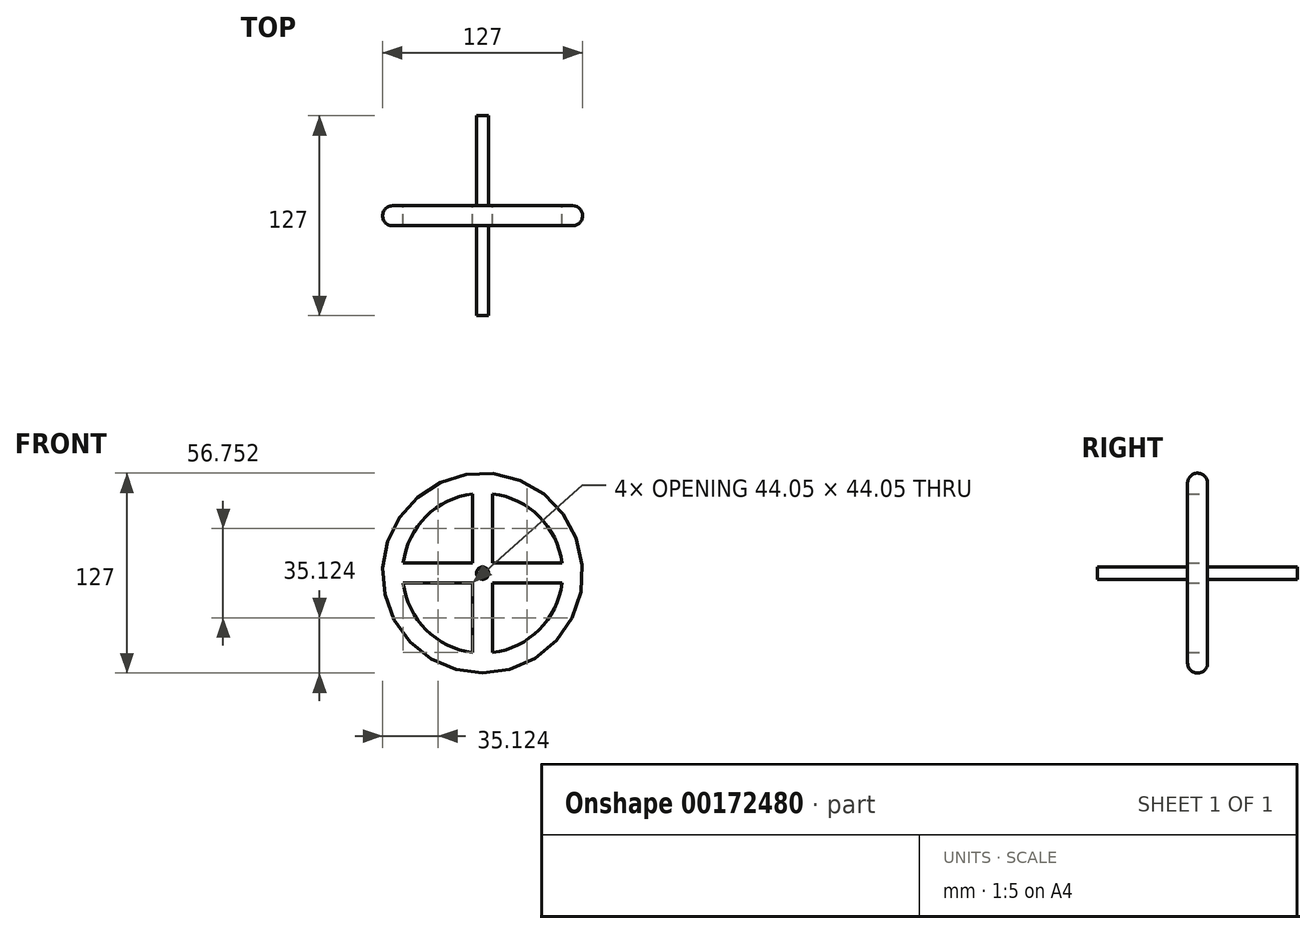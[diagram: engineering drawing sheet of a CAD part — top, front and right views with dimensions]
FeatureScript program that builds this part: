
annotation { "Feature Type Name" : "Feature", "Feature Type Description" : "" }
export const myFeature = defineFeature(function(context is Context, id is Id, definition is map)
    precondition{}
    {
        {
            var Q0;
            Q0=qCreatedBy(makeId("Front.planeOp"),FACE);
            var sketch = newSketch(context, id + "F0", { "sketchPlane" : qUnion([Q0])});
            skCircle(sketch, "E0", {"center": v(0, 0) * mm, "radius": 63.5 * mm});
            skArc(sketch, "E1", {"start": v(-50.4, -6.35) * mm, "mid": v(-35.92, -35.92) * mm, "end": v(-6.35, -50.4) * mm});
            skCircle(sketch, "E2", {"center": v(0, 0) * mm, "radius": 3.81 * mm});
            skLineSegment(sketch, "E3", {"start": v(0, 0) * mm, "end": v(0, 50.8) * mm, "construction": true});
            skLineSegment(sketch, "E4", {"start": v(0, 0) * mm, "end": v(50.8, 0) * mm, "construction": true});
            skLineSegment(sketch, "E5", {"start": v(0, 0) * mm, "end": v(0, -50.8) * mm, "construction": true});
            skLineSegment(sketch, "E6", {"start": v(0, 0) * mm, "end": v(-50.8, 0) * mm, "construction": true});
            skLineSegment(sketch, "E7.0", {"start": v(-6.35, 6.35) * mm, "end": v(-6.35, 50.4) * mm});
            skLineSegment(sketch, "E8.0", {"start": v(6.35, 6.35) * mm, "end": v(6.35, 50.4) * mm});
            skLineSegment(sketch, "E9.0", {"start": v(6.35, 6.35) * mm, "end": v(50.4, 6.35) * mm});
            skLineSegment(sketch, "E10.0", {"start": v(-6.35, 6.35) * mm, "end": v(-50.4, 6.35) * mm});
            skLineSegment(sketch, "E11.0", {"start": v(6.35, -6.35) * mm, "end": v(50.4, -6.35) * mm});
            skLineSegment(sketch, "E12.0", {"start": v(-6.35, -6.35) * mm, "end": v(-50.4, -6.35) * mm});
            skLineSegment(sketch, "E13.0", {"start": v(-6.35, -6.35) * mm, "end": v(-6.35, -50.4) * mm});
            skLineSegment(sketch, "E14.0", {"start": v(6.35, -6.35) * mm, "end": v(6.35, -50.4) * mm});
            skArc(sketch, "E15.trimOffspring", {"start": v(6.35, -50.4) * mm, "mid": v(35.92, -35.92) * mm, "end": v(50.4, -6.35) * mm});
            skArc(sketch, "E16.trimOffspring", {"start": v(50.4, 6.35) * mm, "mid": v(35.92, 35.92) * mm, "end": v(6.35, 50.4) * mm});
            skArc(sketch, "E17.trimOffspring", {"start": v(-6.35, 50.4) * mm, "mid": v(-35.92, 35.92) * mm, "end": v(-50.4, 6.35) * mm});
            skSolve(sketch);
        }
        {
            var Q0;
            Q0=makeQuery(id+"F0.imprint","IMPRINT",FACE,{"disambiguationData":[TD([[makeQuery(id+"F0.imprint","IMPRINT",EDGE,{"derivedFrom":sQuery(id+"F0.wireOp",EDGE,"E0")}),1.0]])]});
            extrude(context, id + "F1", {"entities" : qUnion([Q0]), "endBound" : BoundingType.SYMMETRIC, "depth" : 12.7 * mm});
        }
        {
            var Q0;
            Q0=makeQuery(id+"F1.opExtrude","SWEPT_FACE",FACE,{"disambiguationData":[OSD([sQuery(id+"F0.wireOp",EDGE,"E0")])]});
            fillet(context, id + "F2", {"entities" : qUnion([Q0]), "radius" : 6.35 * mm, "tangentPropagation" : true, "allowEdgeOverflow" : false});
        }
        {
            var Q0;
            Q0=qCreatedBy(makeId("Front.planeOp"),FACE);
            var sketch = newSketch(context, id + "F3", { "sketchPlane" : qUnion([Q0])});
            skCircle(sketch, "E18", {"center": v(0, 0) * mm, "radius": 3.9 * mm});
            skSolve(sketch);
        }
        {
            var Q0;
            Q0=makeQuery(id+"F3.imprint","IMPRINT",FACE,{"disambiguationData":[TD([[makeQuery(id+"F3.imprint","IMPRINT",EDGE,{"derivedFrom":sQuery(id+"F3.wireOp",EDGE,"E18")}),1.0]])]});
            extrude(context, id + "F4", {"entities" : qUnion([Q0]), "operationType" : NewBodyOperationType.ADD, "endBound" : BoundingType.SYMMETRIC, "depth" : 127 * mm});
        }
    });
